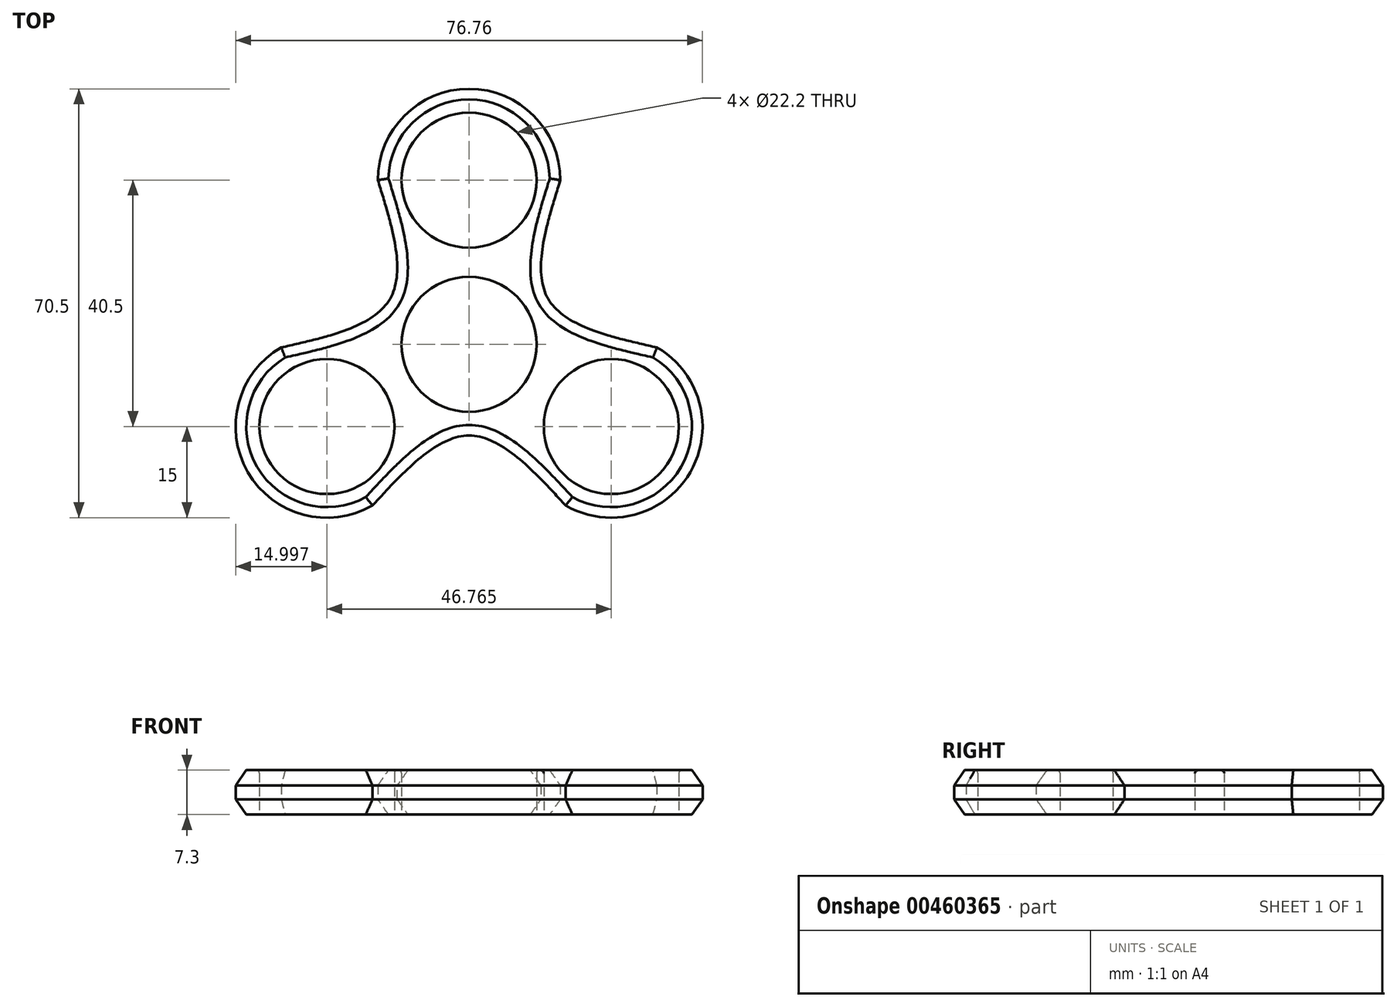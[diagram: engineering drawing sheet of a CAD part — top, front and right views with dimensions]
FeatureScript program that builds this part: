
annotation { "Feature Type Name" : "Feature", "Feature Type Description" : "" }
export const myFeature = defineFeature(function(context is Context, id is Id, definition is map)
    precondition{}
    {
        {
            var Q0;
            Q0=qCreatedBy(makeId("Top.planeOp"),FACE);
            var sketch = newSketch(context, id + "F0", { "sketchPlane" : qUnion([Q0])});
            skCircle(sketch, "E0", {"center": v(0, 0) * mm, "radius": 11.1 * mm});
            skCircle(sketch, "E1", {"center": v(0, 0) * mm, "radius": 15 * mm});
            skLineSegment(sketch, "E2", {"start": v(0, 0) * mm, "end": v(0, 27) * mm});
            skCircle(sketch, "E3", {"center": v(0, 27) * mm, "radius": 15 * mm});
            skCircle(sketch, "E4", {"center": v(0, 27) * mm, "radius": 11.1 * mm});
            skCircle(sketch, "E5.1.0", {"center": v(-23.38, -13.5) * mm, "radius": 15 * mm});
            skCircle(sketch, "E5.1.1", {"center": v(-23.38, -13.5) * mm, "radius": 11.1 * mm});
            skLineSegment(sketch, "E5.1.2", {"start": v(0, 0) * mm, "end": v(-23.38, -13.5) * mm});
            skCircle(sketch, "E5.2.0", {"center": v(23.38, -13.5) * mm, "radius": 15 * mm});
            skCircle(sketch, "E5.2.1", {"center": v(23.38, -13.5) * mm, "radius": 11.1 * mm});
            skLineSegment(sketch, "E5.2.2", {"start": v(0, 0) * mm, "end": v(23.38, -13.5) * mm});
            skLineSegment(sketch, "E6", {"start": v(-23.38, -13.5) * mm, "end": v(-30.88, -0.5) * mm});
            skLineSegment(sketch, "E7", {"start": v(-30.88, -0.5) * mm, "end": v(-15.88, -26.5) * mm});
            skLineSegment(sketch, "E8", {"start": v(23.38, -13.5) * mm, "end": v(30.88, -0.5) * mm});
            skLineSegment(sketch, "E9", {"start": v(30.88, -0.5) * mm, "end": v(15.88, -26.5) * mm});
            skLineSegment(sketch, "E10", {"start": v(0, 27) * mm, "end": v(15, 27) * mm});
            skLineSegment(sketch, "E11", {"start": v(15, 27) * mm, "end": v(-15, 27) * mm});
            skLineSegment(sketch, "E12", {"start": v(0, 0) * mm, "end": v(-13, 7.5) * mm});
            skLineSegment(sketch, "E13", {"start": v(-13, 7.5) * mm, "end": v(0, 0) * mm});
            skLineSegment(sketch, "E14", {"start": v(0, 0) * mm, "end": v(0, -15) * mm});
            skLineSegment(sketch, "E15", {"start": v(0, 0) * mm, "end": v(13, 7.5) * mm});
            skFitSpline(sketch, "E16", {"points": [v(-30.88, -0.5) * mm, v(-13, 7.5) * mm, v(-15, 27) * mm], "startDerivative": vector(45.74, 10.27) * mm, "endDerivative": vector(-13.97, 44.75) * mm});
            skFitSpline(sketch, "E17", {"points": [v(-15.88, -26.5) * mm, v(0, -15) * mm, v(15.88, -26.5) * mm], "startDerivative": vector(31.77, 34.47) * mm, "endDerivative": vector(31.77, -34.47) * mm});
            skFitSpline(sketch, "E18", {"points": [v(30.88, -0.5) * mm, v(13, 7.5) * mm, v(15, 27) * mm], "startDerivative": vector(-45.74, 10.27) * mm, "endDerivative": vector(13.97, 44.75) * mm});
            skLineSegment(sketch, "E19", {"start": v(0, 27) * mm, "end": v(0, 42) * mm});
            skLineSegment(sketch, "E20", {"start": v(-23.38, -13.5) * mm, "end": v(-38.38, -13.5) * mm});
            skLineSegment(sketch, "E21", {"start": v(23.38, -13.5) * mm, "end": v(38.38, -13.5) * mm});
            skLineSegment(sketch, "E22", {"start": v(-23.38, -13.5) * mm, "end": v(-23.38, -28.5) * mm});
            skLineSegment(sketch, "E23", {"start": v(23.38, -13.5) * mm, "end": v(23.38, -28.5) * mm});
            skLineSegment(sketch, "E24", {"start": v(-38.38, -28.5) * mm, "end": v(-38.38, 42) * mm});
            skLineSegment(sketch, "E25", {"start": v(-38.38, 42) * mm, "end": v(38.38, 42) * mm});
            skLineSegment(sketch, "E26", {"start": v(38.38, 42) * mm, "end": v(38.38, -28.5) * mm});
            skLineSegment(sketch, "E27", {"start": v(-38.38, -28.5) * mm, "end": v(38.38, -28.5) * mm});
            skSolve(sketch);
        }
        {
            var Q0;
            {var subQ3=sQuery(id+"F0.wireOp",EDGE,"E19");var subQ5=sQuery(id+"F0.wireOp",EDGE,"E4");var subQ7=makeQuery(id+"F0.imprint","INTERSECT",VERTEX,{"derivedFrom":[subQ5,subQ3]});Q0=makeQuery(id+"F0.imprint","IMPRINT",FACE,{"disambiguationData":[TD([[makeQuery(id+"F0.imprint","IMPRINT",EDGE,{"disambiguationData":[TD([[subQ7,-1.0]])],"derivedFrom":subQ5}),-1.0]])]});}
            var Q1;
            {var subQ3=sQuery(id+"F0.wireOp",EDGE,"E19");var subQ5=sQuery(id+"F0.wireOp",EDGE,"E4");var subQ6=makeQuery(id+"F0.imprint","INTERSECT",VERTEX,{"derivedFrom":[subQ5,subQ3]});Q1=makeQuery(id+"F0.imprint","IMPRINT",FACE,{"disambiguationData":[TD([[makeQuery(id+"F0.imprint","IMPRINT",EDGE,{"disambiguationData":[TD([[subQ6,1.0]])],"derivedFrom":subQ5}),-1.0]])]});}
            var Q2;
            {var subQ5=sQuery(id+"F0.wireOp",EDGE,"E3");var subQ6=sQuery(id+"F0.wireOp",EDGE,"E1");var subQ7=makeQuery(id+"F0.imprint","INTERSECT",VERTEX,{"disambiguationData":[OD(0.0)],"derivedFrom":[subQ6,subQ5]});Q2=makeQuery(id+"F0.imprint","IMPRINT",FACE,{"disambiguationData":[TD([[makeQuery(id+"F0.imprint","IMPRINT",EDGE,{"disambiguationData":[TD([[subQ7,-1.0]])],"derivedFrom":subQ6}),-1.0]])]});}
            var Q3;
            {var subQ1=sQuery(id+"F0.wireOp",EDGE,"E1");var subQ3=sQuery(id+"F0.wireOp",EDGE,"E3");var subQ4=makeQuery(id+"F0.imprint","INTERSECT",VERTEX,{"disambiguationData":[OD(1.0)],"derivedFrom":[subQ1,subQ3]});Q3=makeQuery(id+"F0.imprint","IMPRINT",FACE,{"disambiguationData":[TD([[makeQuery(id+"F0.imprint","IMPRINT",EDGE,{"disambiguationData":[TD([[subQ4,1.0]])],"derivedFrom":subQ3}),-1.0]])]});}
            var Q4;
            {var subQ1=sQuery(id+"F0.wireOp",EDGE,"E1");var subQ3=sQuery(id+"F0.wireOp",EDGE,"E5.1.0");var subQ4=makeQuery(id+"F0.imprint","INTERSECT",VERTEX,{"disambiguationData":[OD(0.0)],"derivedFrom":[subQ1,subQ3]});Q4=makeQuery(id+"F0.imprint","IMPRINT",FACE,{"disambiguationData":[TD([[makeQuery(id+"F0.imprint","IMPRINT",EDGE,{"disambiguationData":[TD([[subQ4,-1.0]])],"derivedFrom":subQ3}),-1.0]])]});}
            var Q5;
            {var subQ5=sQuery(id+"F0.wireOp",EDGE,"E13");var subQ7=sQuery(id+"F0.wireOp",EDGE,"E0");var subQ8=makeQuery(id+"F0.imprint","INTERSECT",VERTEX,{"derivedFrom":[subQ7,subQ5]});Q5=makeQuery(id+"F0.imprint","IMPRINT",FACE,{"disambiguationData":[TD([[makeQuery(id+"F0.imprint","IMPRINT",EDGE,{"disambiguationData":[TD([[subQ8,-1.0]])],"derivedFrom":subQ7}),-1.0]])]});}
            var Q6;
            {var subQ3=sQuery(id+"F0.wireOp",EDGE,"E2");var subQ5=sQuery(id+"F0.wireOp",EDGE,"E0");var subQ6=makeQuery(id+"F0.imprint","INTERSECT",VERTEX,{"derivedFrom":[subQ5,subQ3]});Q6=makeQuery(id+"F0.imprint","IMPRINT",FACE,{"disambiguationData":[TD([[makeQuery(id+"F0.imprint","IMPRINT",EDGE,{"disambiguationData":[TD([[subQ6,-1.0]])],"derivedFrom":subQ5}),-1.0]])]});}
            var Q7;
            {var subQ0=sQuery(id+"F0.wireOp",EDGE,"E2");var subQ1=sQuery(id+"F0.wireOp",EDGE,"E1");var subQ2=makeQuery(id+"F0.imprint","INTERSECT",VERTEX,{"derivedFrom":[subQ1,subQ0]});Q7=makeQuery(id+"F0.imprint","IMPRINT",FACE,{"disambiguationData":[TD([[makeQuery(id+"F0.imprint","IMPRINT",EDGE,{"disambiguationData":[TD([[subQ2,-1.0]])],"derivedFrom":subQ1}),1.0]])]});}
            var Q8;
            {var subQ0=sQuery(id+"F0.wireOp",EDGE,"E3");var subQ1=sQuery(id+"F0.wireOp",EDGE,"E1");var subQ2=makeQuery(id+"F0.imprint","INTERSECT",VERTEX,{"disambiguationData":[OD(0.0)],"derivedFrom":[subQ1,subQ0]});Q8=makeQuery(id+"F0.imprint","IMPRINT",FACE,{"disambiguationData":[TD([[makeQuery(id+"F0.imprint","IMPRINT",EDGE,{"disambiguationData":[TD([[subQ2,-1.0]])],"derivedFrom":subQ1}),1.0]])]});}
            var Q9;
            {var subQ3=sQuery(id+"F0.wireOp",EDGE,"E2");var subQ7=sQuery(id+"F0.wireOp",EDGE,"E0");var subQ8=makeQuery(id+"F0.imprint","INTERSECT",VERTEX,{"derivedFrom":[subQ7,subQ3]});Q9=makeQuery(id+"F0.imprint","IMPRINT",FACE,{"disambiguationData":[TD([[makeQuery(id+"F0.imprint","IMPRINT",EDGE,{"disambiguationData":[TD([[subQ8,1.0]])],"derivedFrom":subQ7}),-1.0]])]});}
            var Q10;
            {var subQ1=sQuery(id+"F0.wireOp",EDGE,"E1");var subQ3=sQuery(id+"F0.wireOp",EDGE,"E3");var subQ4=makeQuery(id+"F0.imprint","INTERSECT",VERTEX,{"disambiguationData":[OD(0.0)],"derivedFrom":[subQ1,subQ3]});Q10=makeQuery(id+"F0.imprint","IMPRINT",FACE,{"disambiguationData":[TD([[makeQuery(id+"F0.imprint","IMPRINT",EDGE,{"disambiguationData":[TD([[subQ4,-1.0]])],"derivedFrom":subQ3}),-1.0]])]});}
            var Q11;
            {var subQ1=sQuery(id+"F0.wireOp",EDGE,"E0");var subQ7=sQuery(id+"F0.wireOp",EDGE,"E15");var subQ9=makeQuery(id+"F0.imprint","INTERSECT",VERTEX,{"derivedFrom":[subQ1,subQ7]});Q11=makeQuery(id+"F0.imprint","IMPRINT",FACE,{"disambiguationData":[TD([[makeQuery(id+"F0.imprint","IMPRINT",EDGE,{"disambiguationData":[TD([[subQ9,1.0]])],"derivedFrom":subQ1}),-1.0]])]});}
            var Q12;
            {var subQ0=sQuery(id+"F0.wireOp",EDGE,"E5.2.2");var subQ1=sQuery(id+"F0.wireOp",EDGE,"E1");var subQ2=makeQuery(id+"F0.imprint","INTERSECT",VERTEX,{"derivedFrom":[subQ1,subQ0]});Q12=makeQuery(id+"F0.imprint","IMPRINT",FACE,{"disambiguationData":[TD([[makeQuery(id+"F0.imprint","IMPRINT",EDGE,{"disambiguationData":[TD([[subQ2,-1.0]])],"derivedFrom":subQ1}),1.0]])]});}
            var Q13;
            {var subQ0=sQuery(id+"F0.wireOp",EDGE,"E5.2.0");var subQ1=sQuery(id+"F0.wireOp",EDGE,"E1");var subQ2=makeQuery(id+"F0.imprint","INTERSECT",VERTEX,{"disambiguationData":[OD(0.0)],"derivedFrom":[subQ1,subQ0]});Q13=makeQuery(id+"F0.imprint","IMPRINT",FACE,{"disambiguationData":[TD([[makeQuery(id+"F0.imprint","IMPRINT",EDGE,{"disambiguationData":[TD([[subQ2,-1.0]])],"derivedFrom":subQ1}),1.0]])]});}
            var Q14;
            {var subQ0=sQuery(id+"F0.wireOp",EDGE,"E5.1.2");var subQ1=sQuery(id+"F0.wireOp",EDGE,"E0");var subQ2=makeQuery(id+"F0.imprint","INTERSECT",VERTEX,{"derivedFrom":[subQ1,subQ0]});Q14=makeQuery(id+"F0.imprint","IMPRINT",FACE,{"disambiguationData":[TD([[makeQuery(id+"F0.imprint","IMPRINT",EDGE,{"disambiguationData":[TD([[subQ2,-1.0]])],"derivedFrom":subQ1}),-1.0]])]});}
            var Q15;
            {var subQ5=sQuery(id+"F0.wireOp",EDGE,"E0");var subQ7=sQuery(id+"F0.wireOp",EDGE,"E14");var subQ9=makeQuery(id+"F0.imprint","INTERSECT",VERTEX,{"derivedFrom":[subQ5,subQ7]});Q15=makeQuery(id+"F0.imprint","IMPRINT",FACE,{"disambiguationData":[TD([[makeQuery(id+"F0.imprint","IMPRINT",EDGE,{"disambiguationData":[TD([[subQ9,-1.0]])],"derivedFrom":subQ5}),-1.0]])]});}
            var Q16;
            {var subQ0=sQuery(id+"F0.wireOp",EDGE,"E5.1.2");var subQ1=sQuery(id+"F0.wireOp",EDGE,"E1");var subQ2=makeQuery(id+"F0.imprint","INTERSECT",VERTEX,{"derivedFrom":[subQ1,subQ0]});Q16=makeQuery(id+"F0.imprint","IMPRINT",FACE,{"disambiguationData":[TD([[makeQuery(id+"F0.imprint","IMPRINT",EDGE,{"disambiguationData":[TD([[subQ2,-1.0]])],"derivedFrom":subQ1}),1.0]])]});}
            var Q17;
            {var subQ0=sQuery(id+"F0.wireOp",EDGE,"E5.1.0");var subQ1=sQuery(id+"F0.wireOp",EDGE,"E1");var subQ2=makeQuery(id+"F0.imprint","INTERSECT",VERTEX,{"disambiguationData":[OD(0.0)],"derivedFrom":[subQ1,subQ0]});Q17=makeQuery(id+"F0.imprint","IMPRINT",FACE,{"disambiguationData":[TD([[makeQuery(id+"F0.imprint","IMPRINT",EDGE,{"disambiguationData":[TD([[subQ2,-1.0]])],"derivedFrom":subQ1}),1.0]])]});}
            var Q18;
            {var subQ5=sQuery(id+"F0.wireOp",EDGE,"E1");var subQ7=sQuery(id+"F0.wireOp",EDGE,"E5.1.0");var subQ8=makeQuery(id+"F0.imprint","INTERSECT",VERTEX,{"disambiguationData":[OD(0.0)],"derivedFrom":[subQ5,subQ7]});Q18=makeQuery(id+"F0.imprint","IMPRINT",FACE,{"disambiguationData":[TD([[makeQuery(id+"F0.imprint","IMPRINT",EDGE,{"disambiguationData":[TD([[subQ8,-1.0]])],"derivedFrom":subQ5}),-1.0]])]});}
            var Q19;
            {var subQ3=sQuery(id+"F0.wireOp",EDGE,"E20");var subQ5=sQuery(id+"F0.wireOp",EDGE,"E5.1.1");var subQ6=makeQuery(id+"F0.imprint","INTERSECT",VERTEX,{"derivedFrom":[subQ5,subQ3]});Q19=makeQuery(id+"F0.imprint","IMPRINT",FACE,{"disambiguationData":[TD([[makeQuery(id+"F0.imprint","IMPRINT",EDGE,{"disambiguationData":[TD([[subQ6,1.0]])],"derivedFrom":subQ5}),-1.0]])]});}
            var Q20;
            {var subQ0=sQuery(id+"F0.wireOp",EDGE,"E20");var subQ5=sQuery(id+"F0.wireOp",EDGE,"E5.1.1");var subQ6=makeQuery(id+"F0.imprint","INTERSECT",VERTEX,{"derivedFrom":[subQ5,subQ0]});Q20=makeQuery(id+"F0.imprint","IMPRINT",FACE,{"disambiguationData":[TD([[makeQuery(id+"F0.imprint","IMPRINT",EDGE,{"disambiguationData":[TD([[subQ6,-1.0]])],"derivedFrom":subQ5}),-1.0]])]});}
            var Q21;
            {var subQ3=sQuery(id+"F0.wireOp",EDGE,"E22");var subQ5=sQuery(id+"F0.wireOp",EDGE,"E5.1.1");var subQ6=makeQuery(id+"F0.imprint","INTERSECT",VERTEX,{"derivedFrom":[subQ5,subQ3]});Q21=makeQuery(id+"F0.imprint","IMPRINT",FACE,{"disambiguationData":[TD([[makeQuery(id+"F0.imprint","IMPRINT",EDGE,{"disambiguationData":[TD([[subQ6,-1.0]])],"derivedFrom":subQ5}),-1.0]])]});}
            var Q22;
            {var subQ1=sQuery(id+"F0.wireOp",EDGE,"E1");var subQ5=sQuery(id+"F0.wireOp",EDGE,"E5.1.2");var subQ6=makeQuery(id+"F0.imprint","INTERSECT",VERTEX,{"derivedFrom":[subQ1,subQ5]});Q22=makeQuery(id+"F0.imprint","IMPRINT",FACE,{"disambiguationData":[TD([[makeQuery(id+"F0.imprint","IMPRINT",EDGE,{"disambiguationData":[TD([[subQ6,-1.0]])],"derivedFrom":subQ1}),-1.0]])]});}
            var Q23;
            {var subQ1=sQuery(id+"F0.wireOp",EDGE,"E1");var subQ3=sQuery(id+"F0.wireOp",EDGE,"E5.2.0");var subQ4=makeQuery(id+"F0.imprint","INTERSECT",VERTEX,{"disambiguationData":[OD(0.0)],"derivedFrom":[subQ1,subQ3]});Q23=makeQuery(id+"F0.imprint","IMPRINT",FACE,{"disambiguationData":[TD([[makeQuery(id+"F0.imprint","IMPRINT",EDGE,{"disambiguationData":[TD([[subQ4,-1.0]])],"derivedFrom":subQ3}),-1.0]])]});}
            var Q24;
            {var subQ1=sQuery(id+"F0.wireOp",EDGE,"E1");var subQ3=sQuery(id+"F0.wireOp",EDGE,"E5.1.0");var subQ4=makeQuery(id+"F0.imprint","INTERSECT",VERTEX,{"disambiguationData":[OD(1.0)],"derivedFrom":[subQ1,subQ3]});Q24=makeQuery(id+"F0.imprint","IMPRINT",FACE,{"disambiguationData":[TD([[makeQuery(id+"F0.imprint","IMPRINT",EDGE,{"disambiguationData":[TD([[subQ4,1.0]])],"derivedFrom":subQ3}),-1.0]])]});}
            var Q25;
            {var subQ5=sQuery(id+"F0.wireOp",EDGE,"E1");var subQ7=sQuery(id+"F0.wireOp",EDGE,"E5.2.0");var subQ8=makeQuery(id+"F0.imprint","INTERSECT",VERTEX,{"disambiguationData":[OD(0.0)],"derivedFrom":[subQ5,subQ7]});Q25=makeQuery(id+"F0.imprint","IMPRINT",FACE,{"disambiguationData":[TD([[makeQuery(id+"F0.imprint","IMPRINT",EDGE,{"disambiguationData":[TD([[subQ8,-1.0]])],"derivedFrom":subQ5}),-1.0]])]});}
            var Q26;
            {var subQ1=sQuery(id+"F0.wireOp",EDGE,"E1");var subQ5=sQuery(id+"F0.wireOp",EDGE,"E5.2.2");var subQ6=makeQuery(id+"F0.imprint","INTERSECT",VERTEX,{"derivedFrom":[subQ1,subQ5]});Q26=makeQuery(id+"F0.imprint","IMPRINT",FACE,{"disambiguationData":[TD([[makeQuery(id+"F0.imprint","IMPRINT",EDGE,{"disambiguationData":[TD([[subQ6,-1.0]])],"derivedFrom":subQ1}),-1.0]])]});}
            var Q27;
            {var subQ1=sQuery(id+"F0.wireOp",EDGE,"E1");var subQ3=sQuery(id+"F0.wireOp",EDGE,"E5.2.0");var subQ4=makeQuery(id+"F0.imprint","INTERSECT",VERTEX,{"disambiguationData":[OD(1.0)],"derivedFrom":[subQ1,subQ3]});Q27=makeQuery(id+"F0.imprint","IMPRINT",FACE,{"disambiguationData":[TD([[makeQuery(id+"F0.imprint","IMPRINT",EDGE,{"disambiguationData":[TD([[subQ4,1.0]])],"derivedFrom":subQ3}),-1.0]])]});}
            var Q28;
            {var subQ3=sQuery(id+"F0.wireOp",EDGE,"E21");var subQ5=sQuery(id+"F0.wireOp",EDGE,"E5.2.1");var subQ6=makeQuery(id+"F0.imprint","INTERSECT",VERTEX,{"derivedFrom":[subQ5,subQ3]});Q28=makeQuery(id+"F0.imprint","IMPRINT",FACE,{"disambiguationData":[TD([[makeQuery(id+"F0.imprint","IMPRINT",EDGE,{"disambiguationData":[TD([[subQ6,-1.0]])],"derivedFrom":subQ5}),-1.0]])]});}
            var Q29;
            {var subQ3=sQuery(id+"F0.wireOp",EDGE,"E23");var subQ5=sQuery(id+"F0.wireOp",EDGE,"E5.2.1");var subQ6=makeQuery(id+"F0.imprint","INTERSECT",VERTEX,{"derivedFrom":[subQ5,subQ3]});Q29=makeQuery(id+"F0.imprint","IMPRINT",FACE,{"disambiguationData":[TD([[makeQuery(id+"F0.imprint","IMPRINT",EDGE,{"disambiguationData":[TD([[subQ6,-1.0]])],"derivedFrom":subQ5}),-1.0]])]});}
            var Q30;
            {var subQ3=sQuery(id+"F0.wireOp",EDGE,"E23");var subQ5=sQuery(id+"F0.wireOp",EDGE,"E5.2.1");var subQ6=makeQuery(id+"F0.imprint","INTERSECT",VERTEX,{"derivedFrom":[subQ5,subQ3]});Q30=makeQuery(id+"F0.imprint","IMPRINT",FACE,{"disambiguationData":[TD([[makeQuery(id+"F0.imprint","IMPRINT",EDGE,{"disambiguationData":[TD([[subQ6,1.0]])],"derivedFrom":subQ5}),-1.0]])]});}
            var Q31;
            {var subQ1=sQuery(id+"F0.wireOp",EDGE,"E1");var subQ5=sQuery(id+"F0.wireOp",EDGE,"E2");var subQ6=makeQuery(id+"F0.imprint","INTERSECT",VERTEX,{"derivedFrom":[subQ1,subQ5]});Q31=makeQuery(id+"F0.imprint","IMPRINT",FACE,{"disambiguationData":[TD([[makeQuery(id+"F0.imprint","IMPRINT",EDGE,{"disambiguationData":[TD([[subQ6,-1.0]])],"derivedFrom":subQ1}),-1.0]])]});}
            extrude(context, id + "F1", {"entities" : qUnion([Q0, Q1, Q2, Q3, Q4, Q5, Q6, Q7, Q8, Q9, Q10, Q11, Q12, Q13, Q14, Q15, Q16, Q17, Q18, Q19, Q20, Q21, Q22, Q23, Q24, Q25, Q26, Q27, Q28, Q29, Q30, Q31]), "depth" : 7.3 * mm, "offsetDistance" : 25 * mm});
        }
        {
            var Q0;
            Q0=makeQuery(id+"F1.opExtrude","CAP_EDGE",EDGE,{"disambiguationData":[OSD([sQuery(id+"F0.wireOp",EDGE,"E0")])],"isStart":false});
            var Q1;
            Q1=makeQuery(id+"F1.opExtrude","CAP_EDGE",EDGE,{"disambiguationData":[OSD([sQuery(id+"F0.wireOp",EDGE,"E5.2.1")])],"isStart":false});
            var Q2;
            Q2=makeQuery(id+"F1.opExtrude","CAP_EDGE",EDGE,{"disambiguationData":[OSD([sQuery(id+"F0.wireOp",EDGE,"E4")])],"isStart":false});
            var Q3;
            Q3=makeQuery(id+"F1.opExtrude","CAP_EDGE",EDGE,{"disambiguationData":[OSD([sQuery(id+"F0.wireOp",EDGE,"E5.1.1")])],"isStart":false});
            fillet(context, id + "F2", {"entities" : qUnion([Q0, Q1, Q2, Q3]), "radius" : 0.5 * mm, "tangentPropagation" : true, "allowEdgeOverflow" : false});
        }
        {
            var Q0;
            Q0=makeQuery(id+"F1.opExtrude","CAP_EDGE",EDGE,{"disambiguationData":[OSD([sQuery(id+"F0.wireOp",EDGE,"E5.2.0")])],"isStart":false});
            var Q1;
            Q1=makeQuery(id+"F1.opExtrude","CAP_EDGE",EDGE,{"disambiguationData":[OSD([sQuery(id+"F0.wireOp",EDGE,"E17")])],"isStart":false});
            var Q2;
            Q2=makeQuery(id+"F1.opExtrude","CAP_EDGE",EDGE,{"disambiguationData":[OSD([sQuery(id+"F0.wireOp",EDGE,"E5.1.0")])],"isStart":false});
            var Q3;
            Q3=makeQuery(id+"F1.opExtrude","CAP_EDGE",EDGE,{"disambiguationData":[OSD([sQuery(id+"F0.wireOp",EDGE,"E16")])],"isStart":false});
            var Q4;
            Q4=makeQuery(id+"F1.opExtrude","CAP_EDGE",EDGE,{"disambiguationData":[OSD([sQuery(id+"F0.wireOp",EDGE,"E3")])],"isStart":false});
            var Q5;
            Q5=makeQuery(id+"F1.opExtrude","CAP_EDGE",EDGE,{"disambiguationData":[OSD([sQuery(id+"F0.wireOp",EDGE,"E18")])],"isStart":false});
            chamfer(context, id + "F3", {"entities" : qUnion([Q0, Q1, Q2, Q3, Q4, Q5]), "chamferType" : ChamferType.OFFSET_ANGLE, "width" : 2.5 * mm, "oppositeDirection" : true, "angle" : 35 * degree, "tangentPropagation" : true});
        }
        {
            var Q0;
            Q0=makeQuery(id+"F1.opExtrude","CAP_EDGE",EDGE,{"disambiguationData":[OSD([sQuery(id+"F0.wireOp",EDGE,"E5.1.0")])],"isStart":true});
            var Q1;
            Q1=makeQuery(id+"F1.opExtrude","CAP_EDGE",EDGE,{"disambiguationData":[OSD([sQuery(id+"F0.wireOp",EDGE,"E17")])],"isStart":true});
            var Q2;
            Q2=makeQuery(id+"F1.opExtrude","CAP_EDGE",EDGE,{"disambiguationData":[OSD([sQuery(id+"F0.wireOp",EDGE,"E16")])],"isStart":true});
            var Q3;
            Q3=makeQuery(id+"F1.opExtrude","CAP_EDGE",EDGE,{"disambiguationData":[OSD([sQuery(id+"F0.wireOp",EDGE,"E3")])],"isStart":true});
            var Q4;
            Q4=makeQuery(id+"F1.opExtrude","CAP_EDGE",EDGE,{"disambiguationData":[OSD([sQuery(id+"F0.wireOp",EDGE,"E5.2.0")])],"isStart":true});
            var Q5;
            Q5=makeQuery(id+"F1.opExtrude","CAP_EDGE",EDGE,{"disambiguationData":[OSD([sQuery(id+"F0.wireOp",EDGE,"E18")])],"isStart":true});
            chamfer(context, id + "F4", {"entities" : qUnion([Q0, Q1, Q2, Q3, Q4, Q5]), "chamferType" : ChamferType.OFFSET_ANGLE, "width" : 2.5 * mm, "oppositeDirection" : false, "angle" : 35 * degree, "tangentPropagation" : true});
        }
    });
